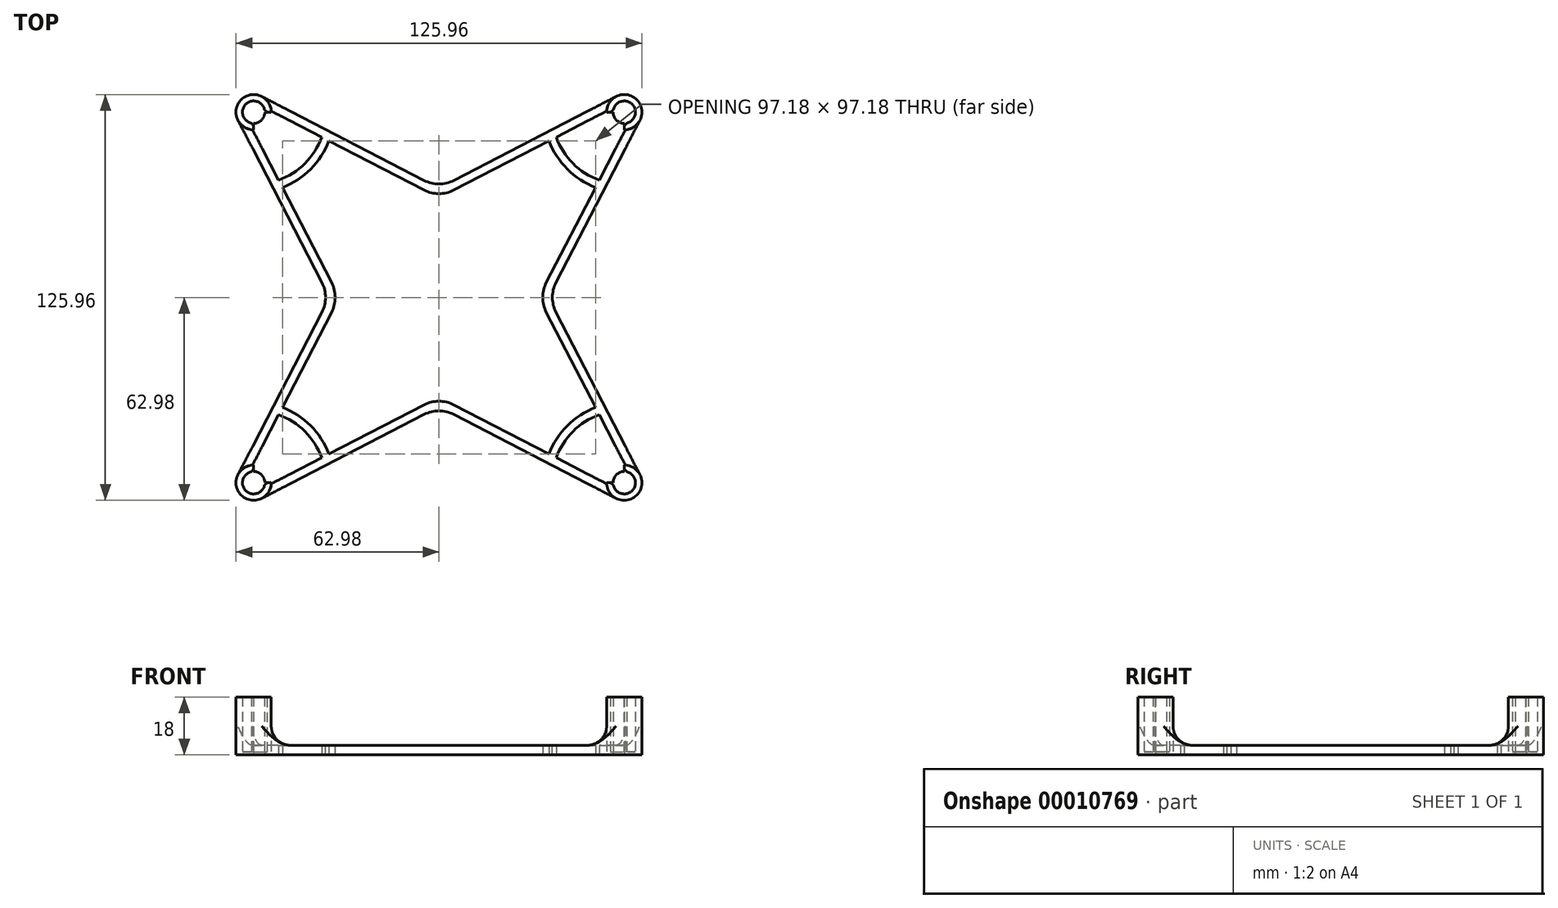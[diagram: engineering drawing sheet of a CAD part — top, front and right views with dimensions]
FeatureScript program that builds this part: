
annotation { "Feature Type Name" : "Feature", "Feature Type Description" : "" }
export const myFeature = defineFeature(function(context is Context, id is Id, definition is map)
    precondition{}
    {
        {
            var Q0;
            Q0=qCreatedBy(makeId("Top.planeOp"),FACE);
            var sketch = newSketch(context, id + "F0", { "sketchPlane" : qUnion([Q0])});
            skLineSegment(sketch, "E0.rect.bottom", {"start": v(57.5, 57.5) * mm, "end": v(-57.5, 57.5) * mm});
            skLineSegment(sketch, "E0.rect.top", {"start": v(57.5, -57.5) * mm, "end": v(-57.5, -57.5) * mm});
            skLineSegment(sketch, "E0.rect.left", {"start": v(57.5, 57.5) * mm, "end": v(57.5, -57.5) * mm});
            skLineSegment(sketch, "E0.rect.right", {"start": v(-57.5, 57.5) * mm, "end": v(-57.5, -57.5) * mm});
            skPoint(sketch, "E0.rect.middle", {"position": v(0, 0) * mm});
            skLineSegment(sketch, "E1", {"start": v(0, 33.94) * mm, "end": v(-33.94, 0) * mm});
            skLineSegment(sketch, "E2", {"start": v(-33.94, 0) * mm, "end": v(0, -33.94) * mm});
            skLineSegment(sketch, "E3", {"start": v(0, -33.94) * mm, "end": v(33.94, 0) * mm});
            skLineSegment(sketch, "E4", {"start": v(33.94, 0) * mm, "end": v(0, 33.94) * mm});
            skCircle(sketch, "E5", {"center": v(57.5, 57.5) * mm, "radius": 3.48 * mm});
            skCircle(sketch, "E6", {"center": v(57.5, 57.5) * mm, "radius": 5.47 * mm});
            skLineSegment(sketch, "E7", {"start": v(57.5, 60.98) * mm, "end": v(57.5, 62.98) * mm, "construction": true});
            skCircle(sketch, "E8", {"center": v(-57.5, 57.5) * mm, "radius": 3.48 * mm});
            skCircle(sketch, "E9", {"center": v(-57.5, 57.5) * mm, "radius": 5.47 * mm});
            skCircle(sketch, "E10", {"center": v(-57.5, -57.5) * mm, "radius": 3.48 * mm});
            skCircle(sketch, "E11", {"center": v(-57.5, -57.5) * mm, "radius": 5.47 * mm});
            skCircle(sketch, "E12", {"center": v(57.5, -57.5) * mm, "radius": 3.48 * mm});
            skCircle(sketch, "E13", {"center": v(57.5, -57.5) * mm, "radius": 5.47 * mm});
            skLineSegment(sketch, "E14", {"start": v(62.36, 54.99) * mm, "end": v(33.94, 0) * mm});
            skLineSegment(sketch, "E15", {"start": v(33.94, 0) * mm, "end": v(62.36, -54.99) * mm});
            skLineSegment(sketch, "E16", {"start": v(54.99, -62.36) * mm, "end": v(0, -33.94) * mm});
            skLineSegment(sketch, "E17", {"start": v(0, -33.94) * mm, "end": v(-54.99, -62.36) * mm});
            skLineSegment(sketch, "E18", {"start": v(-62.36, -54.99) * mm, "end": v(-33.94, 0) * mm});
            skLineSegment(sketch, "E19", {"start": v(-33.94, 0) * mm, "end": v(-62.36, 54.99) * mm});
            skLineSegment(sketch, "E20", {"start": v(-54.99, 62.36) * mm, "end": v(0, 33.94) * mm});
            skLineSegment(sketch, "E21", {"start": v(0, 33.94) * mm, "end": v(54.99, 62.36) * mm});
            skLineSegment(sketch, "E22.0", {"start": v(30.94, 0) * mm, "end": v(0, 30.94) * mm});
            skLineSegment(sketch, "E22.1", {"start": v(0, -30.94) * mm, "end": v(30.94, 0) * mm});
            skLineSegment(sketch, "E22.2", {"start": v(-30.94, 0) * mm, "end": v(0, -30.94) * mm});
            skLineSegment(sketch, "E22.3", {"start": v(0, 30.94) * mm, "end": v(-30.94, 0) * mm});
            skLineSegment(sketch, "E23", {"start": v(-30.94, 0) * mm, "end": v(-57.84, 52.04) * mm});
            skLineSegment(sketch, "E24", {"start": v(-30.94, 0) * mm, "end": v(-57.84, -52.04) * mm});
            skLineSegment(sketch, "E25", {"start": v(30.94, 0) * mm, "end": v(33.94, 0) * mm, "construction": true});
            skLineSegment(sketch, "E26", {"start": v(0, -30.94) * mm, "end": v(-52.04, -57.84) * mm});
            skLineSegment(sketch, "E27", {"start": v(0, -30.94) * mm, "end": v(52.04, -57.84) * mm});
            skLineSegment(sketch, "E28", {"start": v(57.84, -52.04) * mm, "end": v(30.94, 0) * mm});
            skLineSegment(sketch, "E29", {"start": v(30.94, 0) * mm, "end": v(57.84, 52.04) * mm});
            skLineSegment(sketch, "E30", {"start": v(52.04, 57.84) * mm, "end": v(0, 30.94) * mm});
            skLineSegment(sketch, "E31", {"start": v(0, 30.94) * mm, "end": v(-52.04, 57.84) * mm});
            skCircle(sketch, "E32", {"center": v(57.5, 57.5) * mm, "radius": 22.5 * mm});
            skCircle(sketch, "E33", {"center": v(57.5, 57.5) * mm, "radius": 25 * mm});
            skLineSegment(sketch, "E34", {"start": v(57.5, 80) * mm, "end": v(57.5, 82.5) * mm, "construction": true});
            skCircle(sketch, "E35", {"center": v(-57.5, 57.5) * mm, "radius": 22.5 * mm});
            skCircle(sketch, "E36", {"center": v(-57.5, 57.5) * mm, "radius": 25 * mm});
            skCircle(sketch, "E37", {"center": v(-57.5, -57.5) * mm, "radius": 22.5 * mm});
            skCircle(sketch, "E38", {"center": v(-57.5, -57.5) * mm, "radius": 25 * mm});
            skCircle(sketch, "E39", {"center": v(57.5, -57.5) * mm, "radius": 22.5 * mm});
            skCircle(sketch, "E40", {"center": v(57.5, -57.5) * mm, "radius": 25 * mm});
            skSolve(sketch);
        }
        {
            var Q0;
            {var subQ1=sQuery(id+"F0.wireOp",EDGE,"E23");var subQ5=sQuery(id+"F0.wireOp",EDGE,"E0.rect.right");var subQ6=makeQuery(id+"F0.imprint","INTERSECT",VERTEX,{"derivedFrom":[subQ5,subQ1]});Q0=makeQuery(id+"F0.imprint","IMPRINT",FACE,{"disambiguationData":[TD([[makeQuery(id+"F0.imprint","IMPRINT",EDGE,{"disambiguationData":[TD([[subQ6,-1.0]])],"derivedFrom":subQ5}),1.0]])]});}
            var Q1;
            {var subQ1=sQuery(id+"F0.wireOp",EDGE,"E0.rect.right");var subQ5=sQuery(id+"F0.wireOp",EDGE,"E23");var subQ6=makeQuery(id+"F0.imprint","INTERSECT",VERTEX,{"derivedFrom":[subQ1,subQ5]});Q1=makeQuery(id+"F0.imprint","IMPRINT",FACE,{"disambiguationData":[TD([[makeQuery(id+"F0.imprint","IMPRINT",EDGE,{"disambiguationData":[TD([[subQ6,-1.0]])],"derivedFrom":subQ1}),-1.0]])]});}
            var Q2;
            {var subQ0=sQuery(id+"F0.wireOp",EDGE,"E9");var subQ7=sQuery(id+"F0.wireOp",EDGE,"E0.rect.bottom");var subQ8=makeQuery(id+"F0.imprint","INTERSECT",VERTEX,{"derivedFrom":[subQ7,subQ0]});Q2=makeQuery(id+"F0.imprint","IMPRINT",FACE,{"disambiguationData":[TD([[makeQuery(id+"F0.imprint","IMPRINT",EDGE,{"disambiguationData":[TD([[subQ8,-1.0]])],"derivedFrom":subQ7}),-1.0]])]});}
            var Q3;
            {var subQ1=sQuery(id+"F0.wireOp",EDGE,"E0.rect.bottom");var subQ5=sQuery(id+"F0.wireOp",EDGE,"E20");var subQ6=makeQuery(id+"F0.imprint","INTERSECT",VERTEX,{"derivedFrom":[subQ1,subQ5]});Q3=makeQuery(id+"F0.imprint","IMPRINT",FACE,{"disambiguationData":[TD([[makeQuery(id+"F0.imprint","IMPRINT",EDGE,{"disambiguationData":[TD([[subQ6,-1.0]])],"derivedFrom":subQ1}),-1.0]])]});}
            var Q4;
            {var subQ3=sQuery(id+"F0.wireOp",EDGE,"E20");var subQ5=sQuery(id+"F0.wireOp",EDGE,"E0.rect.bottom");var subQ7=makeQuery(id+"F0.imprint","INTERSECT",VERTEX,{"derivedFrom":[subQ5,subQ3]});Q4=makeQuery(id+"F0.imprint","IMPRINT",FACE,{"disambiguationData":[TD([[makeQuery(id+"F0.imprint","IMPRINT",EDGE,{"disambiguationData":[TD([[subQ7,-1.0]])],"derivedFrom":subQ5}),1.0]])]});}
            var Q5;
            {var subQ0=sQuery(id+"F0.wireOp",EDGE,"E36");var subQ3=sQuery(id+"F0.wireOp",EDGE,"E19");var subQ4=makeQuery(id+"F0.imprint","INTERSECT",VERTEX,{"derivedFrom":[subQ3,subQ0]});Q5=makeQuery(id+"F0.imprint","IMPRINT",FACE,{"disambiguationData":[TD([[makeQuery(id+"F0.imprint","IMPRINT",EDGE,{"disambiguationData":[TD([[subQ4,-1.0]])],"derivedFrom":subQ3}),-1.0]])]});}
            var Q6;
            {var subQ1=sQuery(id+"F0.wireOp",EDGE,"E23");var subQ5=sQuery(id+"F0.wireOp",EDGE,"E1");var subQ6=makeQuery(id+"F0.imprint","INTERSECT",VERTEX,{"derivedFrom":[subQ5,subQ1]});Q6=makeQuery(id+"F0.imprint","IMPRINT",FACE,{"disambiguationData":[TD([[makeQuery(id+"F0.imprint","IMPRINT",EDGE,{"disambiguationData":[TD([[subQ6,-1.0]])],"derivedFrom":subQ1}),1.0]])]});}
            var Q7;
            {var subQ3=sQuery(id+"F0.wireOp",EDGE,"E20");var subQ5=sQuery(id+"F0.wireOp",EDGE,"E35");var subQ7=makeQuery(id+"F0.imprint","INTERSECT",VERTEX,{"derivedFrom":[subQ3,subQ5]});Q7=makeQuery(id+"F0.imprint","IMPRINT",FACE,{"disambiguationData":[TD([[makeQuery(id+"F0.imprint","IMPRINT",EDGE,{"disambiguationData":[TD([[subQ7,-1.0]])],"derivedFrom":subQ3}),-1.0]])]});}
            var Q8;
            {var subQ1=sQuery(id+"F0.wireOp",EDGE,"E31");var subQ5=sQuery(id+"F0.wireOp",EDGE,"E1");var subQ6=makeQuery(id+"F0.imprint","INTERSECT",VERTEX,{"derivedFrom":[subQ5,subQ1]});Q8=makeQuery(id+"F0.imprint","IMPRINT",FACE,{"disambiguationData":[TD([[makeQuery(id+"F0.imprint","IMPRINT",EDGE,{"disambiguationData":[TD([[subQ6,-1.0]])],"derivedFrom":subQ1}),-1.0]])]});}
            var Q9;
            {var subQ0=sQuery(id+"F0.wireOp",EDGE,"E31");var subQ1=sQuery(id+"F0.wireOp",EDGE,"E1");var subQ2=makeQuery(id+"F0.imprint","INTERSECT",VERTEX,{"derivedFrom":[subQ1,subQ0]});Q9=makeQuery(id+"F0.imprint","IMPRINT",FACE,{"disambiguationData":[TD([[makeQuery(id+"F0.imprint","IMPRINT",EDGE,{"disambiguationData":[TD([[subQ2,1.0]])],"derivedFrom":subQ1}),1.0]])]});}
            var Q10;
            {var subQ1=sQuery(id+"F0.wireOp",EDGE,"E30");var subQ5=sQuery(id+"F0.wireOp",EDGE,"E4");var subQ6=makeQuery(id+"F0.imprint","INTERSECT",VERTEX,{"derivedFrom":[subQ5,subQ1]});Q10=makeQuery(id+"F0.imprint","IMPRINT",FACE,{"disambiguationData":[TD([[makeQuery(id+"F0.imprint","IMPRINT",EDGE,{"disambiguationData":[TD([[subQ6,1.0]])],"derivedFrom":subQ1}),-1.0]])]});}
            var Q11;
            {var subQ0=sQuery(id+"F0.wireOp",EDGE,"E33");var subQ3=sQuery(id+"F0.wireOp",EDGE,"E21");var subQ4=makeQuery(id+"F0.imprint","INTERSECT",VERTEX,{"derivedFrom":[subQ3,subQ0]});Q11=makeQuery(id+"F0.imprint","IMPRINT",FACE,{"disambiguationData":[TD([[makeQuery(id+"F0.imprint","IMPRINT",EDGE,{"disambiguationData":[TD([[subQ4,-1.0]])],"derivedFrom":subQ3}),-1.0]])]});}
            var Q12;
            {var subQ1=sQuery(id+"F0.wireOp",EDGE,"E30");var subQ5=sQuery(id+"F0.wireOp",EDGE,"E0.rect.bottom");var subQ6=makeQuery(id+"F0.imprint","INTERSECT",VERTEX,{"derivedFrom":[subQ5,subQ1]});Q12=makeQuery(id+"F0.imprint","IMPRINT",FACE,{"disambiguationData":[TD([[makeQuery(id+"F0.imprint","IMPRINT",EDGE,{"disambiguationData":[TD([[subQ6,-1.0]])],"derivedFrom":subQ5}),1.0]])]});}
            var Q13;
            {var subQ0=sQuery(id+"F0.wireOp",EDGE,"E30");var subQ1=sQuery(id+"F0.wireOp",EDGE,"E0.rect.bottom");var subQ2=makeQuery(id+"F0.imprint","INTERSECT",VERTEX,{"derivedFrom":[subQ1,subQ0]});Q13=makeQuery(id+"F0.imprint","IMPRINT",FACE,{"disambiguationData":[TD([[makeQuery(id+"F0.imprint","IMPRINT",EDGE,{"disambiguationData":[TD([[subQ2,-1.0]])],"derivedFrom":subQ1}),-1.0]])]});}
            var Q14;
            {var subQ7=sQuery(id+"F0.wireOp",EDGE,"E5");var subQ9=sQuery(id+"F0.wireOp",EDGE,"E0.rect.bottom");var subQ10=makeQuery(id+"F0.imprint","INTERSECT",VERTEX,{"derivedFrom":[subQ9,subQ7]});Q14=makeQuery(id+"F0.imprint","IMPRINT",FACE,{"disambiguationData":[TD([[makeQuery(id+"F0.imprint","IMPRINT",EDGE,{"disambiguationData":[TD([[subQ10,-1.0]])],"derivedFrom":subQ9}),-1.0]])]});}
            var Q15;
            {var subQ0=sQuery(id+"F0.wireOp",EDGE,"E29");var subQ1=sQuery(id+"F0.wireOp",EDGE,"E0.rect.left");var subQ2=makeQuery(id+"F0.imprint","INTERSECT",VERTEX,{"derivedFrom":[subQ1,subQ0]});Q15=makeQuery(id+"F0.imprint","IMPRINT",FACE,{"disambiguationData":[TD([[makeQuery(id+"F0.imprint","IMPRINT",EDGE,{"disambiguationData":[TD([[subQ2,-1.0]])],"derivedFrom":subQ1}),1.0]])]});}
            var Q16;
            {var subQ1=sQuery(id+"F0.wireOp",EDGE,"E29");var subQ5=sQuery(id+"F0.wireOp",EDGE,"E0.rect.left");var subQ6=makeQuery(id+"F0.imprint","INTERSECT",VERTEX,{"derivedFrom":[subQ5,subQ1]});Q16=makeQuery(id+"F0.imprint","IMPRINT",FACE,{"disambiguationData":[TD([[makeQuery(id+"F0.imprint","IMPRINT",EDGE,{"disambiguationData":[TD([[subQ6,-1.0]])],"derivedFrom":subQ5}),-1.0]])]});}
            var Q17;
            {var subQ3=sQuery(id+"F0.wireOp",EDGE,"E14");var subQ5=sQuery(id+"F0.wireOp",EDGE,"E32");var subQ7=makeQuery(id+"F0.imprint","INTERSECT",VERTEX,{"derivedFrom":[subQ3,subQ5]});Q17=makeQuery(id+"F0.imprint","IMPRINT",FACE,{"disambiguationData":[TD([[makeQuery(id+"F0.imprint","IMPRINT",EDGE,{"disambiguationData":[TD([[subQ7,-1.0]])],"derivedFrom":subQ3}),-1.0]])]});}
            var Q18;
            {var subQ1=sQuery(id+"F0.wireOp",EDGE,"E29");var subQ5=sQuery(id+"F0.wireOp",EDGE,"E4");var subQ6=makeQuery(id+"F0.imprint","INTERSECT",VERTEX,{"derivedFrom":[subQ5,subQ1]});Q18=makeQuery(id+"F0.imprint","IMPRINT",FACE,{"disambiguationData":[TD([[makeQuery(id+"F0.imprint","IMPRINT",EDGE,{"disambiguationData":[TD([[subQ6,-1.0]])],"derivedFrom":subQ1}),-1.0]])]});}
            var Q19;
            {var subQ3=sQuery(id+"F0.wireOp",EDGE,"E28");var subQ5=sQuery(id+"F0.wireOp",EDGE,"E3");var subQ6=makeQuery(id+"F0.imprint","INTERSECT",VERTEX,{"derivedFrom":[subQ5,subQ3]});Q19=makeQuery(id+"F0.imprint","IMPRINT",FACE,{"disambiguationData":[TD([[makeQuery(id+"F0.imprint","IMPRINT",EDGE,{"disambiguationData":[TD([[subQ6,-1.0]])],"derivedFrom":subQ5}),1.0]])]});}
            var Q20;
            {var subQ3=sQuery(id+"F0.wireOp",EDGE,"E23");var subQ5=sQuery(id+"F0.wireOp",EDGE,"E1");var subQ6=makeQuery(id+"F0.imprint","INTERSECT",VERTEX,{"derivedFrom":[subQ5,subQ3]});Q20=makeQuery(id+"F0.imprint","IMPRINT",FACE,{"disambiguationData":[TD([[makeQuery(id+"F0.imprint","IMPRINT",EDGE,{"disambiguationData":[TD([[subQ6,-1.0]])],"derivedFrom":subQ5}),1.0]])]});}
            var Q21;
            {var subQ1=sQuery(id+"F0.wireOp",EDGE,"E24");var subQ5=sQuery(id+"F0.wireOp",EDGE,"E2");var subQ6=makeQuery(id+"F0.imprint","INTERSECT",VERTEX,{"derivedFrom":[subQ5,subQ1]});Q21=makeQuery(id+"F0.imprint","IMPRINT",FACE,{"disambiguationData":[TD([[makeQuery(id+"F0.imprint","IMPRINT",EDGE,{"disambiguationData":[TD([[subQ6,-1.0]])],"derivedFrom":subQ1}),-1.0]])]});}
            var Q22;
            {var subQ1=sQuery(id+"F0.wireOp",EDGE,"E28");var subQ5=sQuery(id+"F0.wireOp",EDGE,"E3");var subQ6=makeQuery(id+"F0.imprint","INTERSECT",VERTEX,{"derivedFrom":[subQ5,subQ1]});Q22=makeQuery(id+"F0.imprint","IMPRINT",FACE,{"disambiguationData":[TD([[makeQuery(id+"F0.imprint","IMPRINT",EDGE,{"disambiguationData":[TD([[subQ6,1.0]])],"derivedFrom":subQ1}),-1.0]])]});}
            var Q23;
            {var subQ0=sQuery(id+"F0.wireOp",EDGE,"E40");var subQ3=sQuery(id+"F0.wireOp",EDGE,"E15");var subQ4=makeQuery(id+"F0.imprint","INTERSECT",VERTEX,{"derivedFrom":[subQ3,subQ0]});Q23=makeQuery(id+"F0.imprint","IMPRINT",FACE,{"disambiguationData":[TD([[makeQuery(id+"F0.imprint","IMPRINT",EDGE,{"disambiguationData":[TD([[subQ4,-1.0]])],"derivedFrom":subQ3}),-1.0]])]});}
            var Q24;
            {var subQ3=sQuery(id+"F0.wireOp",EDGE,"E18");var subQ5=sQuery(id+"F0.wireOp",EDGE,"E37");var subQ7=makeQuery(id+"F0.imprint","INTERSECT",VERTEX,{"derivedFrom":[subQ3,subQ5]});Q24=makeQuery(id+"F0.imprint","IMPRINT",FACE,{"disambiguationData":[TD([[makeQuery(id+"F0.imprint","IMPRINT",EDGE,{"disambiguationData":[TD([[subQ7,-1.0]])],"derivedFrom":subQ3}),-1.0]])]});}
            var Q25;
            {var subQ3=sQuery(id+"F0.wireOp",EDGE,"E18");var subQ5=sQuery(id+"F0.wireOp",EDGE,"E0.rect.right");var subQ7=makeQuery(id+"F0.imprint","INTERSECT",VERTEX,{"derivedFrom":[subQ5,subQ3]});Q25=makeQuery(id+"F0.imprint","IMPRINT",FACE,{"disambiguationData":[TD([[makeQuery(id+"F0.imprint","IMPRINT",EDGE,{"disambiguationData":[TD([[subQ7,-1.0]])],"derivedFrom":subQ5}),1.0]])]});}
            var Q26;
            {var subQ1=sQuery(id+"F0.wireOp",EDGE,"E0.rect.right");var subQ5=sQuery(id+"F0.wireOp",EDGE,"E18");var subQ6=makeQuery(id+"F0.imprint","INTERSECT",VERTEX,{"derivedFrom":[subQ1,subQ5]});Q26=makeQuery(id+"F0.imprint","IMPRINT",FACE,{"disambiguationData":[TD([[makeQuery(id+"F0.imprint","IMPRINT",EDGE,{"disambiguationData":[TD([[subQ6,-1.0]])],"derivedFrom":subQ1}),-1.0]])]});}
            var Q27;
            {var subQ0=sQuery(id+"F0.wireOp",EDGE,"E11");var subQ1=sQuery(id+"F0.wireOp",EDGE,"E0.rect.top");var subQ2=makeQuery(id+"F0.imprint","INTERSECT",VERTEX,{"derivedFrom":[subQ1,subQ0]});Q27=makeQuery(id+"F0.imprint","IMPRINT",FACE,{"disambiguationData":[TD([[makeQuery(id+"F0.imprint","IMPRINT",EDGE,{"disambiguationData":[TD([[subQ2,-1.0]])],"derivedFrom":subQ1}),1.0]])]});}
            var Q28;
            {var subQ1=sQuery(id+"F0.wireOp",EDGE,"E0.rect.top");var subQ5=sQuery(id+"F0.wireOp",EDGE,"E17");var subQ6=makeQuery(id+"F0.imprint","INTERSECT",VERTEX,{"derivedFrom":[subQ1,subQ5]});Q28=makeQuery(id+"F0.imprint","IMPRINT",FACE,{"disambiguationData":[TD([[makeQuery(id+"F0.imprint","IMPRINT",EDGE,{"disambiguationData":[TD([[subQ6,-1.0]])],"derivedFrom":subQ1}),1.0]])]});}
            var Q29;
            {var subQ3=sQuery(id+"F0.wireOp",EDGE,"E17");var subQ5=sQuery(id+"F0.wireOp",EDGE,"E0.rect.top");var subQ7=makeQuery(id+"F0.imprint","INTERSECT",VERTEX,{"derivedFrom":[subQ5,subQ3]});Q29=makeQuery(id+"F0.imprint","IMPRINT",FACE,{"disambiguationData":[TD([[makeQuery(id+"F0.imprint","IMPRINT",EDGE,{"disambiguationData":[TD([[subQ7,-1.0]])],"derivedFrom":subQ5}),-1.0]])]});}
            var Q30;
            {var subQ0=sQuery(id+"F0.wireOp",EDGE,"E38");var subQ3=sQuery(id+"F0.wireOp",EDGE,"E17");var subQ4=makeQuery(id+"F0.imprint","INTERSECT",VERTEX,{"derivedFrom":[subQ3,subQ0]});Q30=makeQuery(id+"F0.imprint","IMPRINT",FACE,{"disambiguationData":[TD([[makeQuery(id+"F0.imprint","IMPRINT",EDGE,{"disambiguationData":[TD([[subQ4,-1.0]])],"derivedFrom":subQ3}),-1.0]])]});}
            var Q31;
            {var subQ1=sQuery(id+"F0.wireOp",EDGE,"E26");var subQ5=sQuery(id+"F0.wireOp",EDGE,"E2");var subQ6=makeQuery(id+"F0.imprint","INTERSECT",VERTEX,{"derivedFrom":[subQ5,subQ1]});Q31=makeQuery(id+"F0.imprint","IMPRINT",FACE,{"disambiguationData":[TD([[makeQuery(id+"F0.imprint","IMPRINT",EDGE,{"disambiguationData":[TD([[subQ6,-1.0]])],"derivedFrom":subQ1}),1.0]])]});}
            var Q32;
            {var subQ3=sQuery(id+"F0.wireOp",EDGE,"E26");var subQ5=sQuery(id+"F0.wireOp",EDGE,"E2");var subQ6=makeQuery(id+"F0.imprint","INTERSECT",VERTEX,{"derivedFrom":[subQ5,subQ3]});Q32=makeQuery(id+"F0.imprint","IMPRINT",FACE,{"disambiguationData":[TD([[makeQuery(id+"F0.imprint","IMPRINT",EDGE,{"disambiguationData":[TD([[subQ6,-1.0]])],"derivedFrom":subQ5}),1.0]])]});}
            var Q33;
            {var subQ1=sQuery(id+"F0.wireOp",EDGE,"E27");var subQ5=sQuery(id+"F0.wireOp",EDGE,"E3");var subQ6=makeQuery(id+"F0.imprint","INTERSECT",VERTEX,{"derivedFrom":[subQ5,subQ1]});Q33=makeQuery(id+"F0.imprint","IMPRINT",FACE,{"disambiguationData":[TD([[makeQuery(id+"F0.imprint","IMPRINT",EDGE,{"disambiguationData":[TD([[subQ6,-1.0]])],"derivedFrom":subQ1}),-1.0]])]});}
            var Q34;
            {var subQ3=sQuery(id+"F0.wireOp",EDGE,"E16");var subQ5=sQuery(id+"F0.wireOp",EDGE,"E39");var subQ7=makeQuery(id+"F0.imprint","INTERSECT",VERTEX,{"derivedFrom":[subQ3,subQ5]});Q34=makeQuery(id+"F0.imprint","IMPRINT",FACE,{"disambiguationData":[TD([[makeQuery(id+"F0.imprint","IMPRINT",EDGE,{"disambiguationData":[TD([[subQ7,-1.0]])],"derivedFrom":subQ3}),-1.0]])]});}
            var Q35;
            {var subQ3=sQuery(id+"F0.wireOp",EDGE,"E0.rect.top");var subQ9=sQuery(id+"F0.wireOp",EDGE,"E12");var subQ11=makeQuery(id+"F0.imprint","INTERSECT",VERTEX,{"derivedFrom":[subQ3,subQ9]});Q35=makeQuery(id+"F0.imprint","IMPRINT",FACE,{"disambiguationData":[TD([[makeQuery(id+"F0.imprint","IMPRINT",EDGE,{"disambiguationData":[TD([[subQ11,-1.0]])],"derivedFrom":subQ3}),1.0]])]});}
            var Q36;
            {var subQ1=sQuery(id+"F0.wireOp",EDGE,"E0.rect.top");var subQ5=sQuery(id+"F0.wireOp",EDGE,"E27");var subQ6=makeQuery(id+"F0.imprint","INTERSECT",VERTEX,{"derivedFrom":[subQ1,subQ5]});Q36=makeQuery(id+"F0.imprint","IMPRINT",FACE,{"disambiguationData":[TD([[makeQuery(id+"F0.imprint","IMPRINT",EDGE,{"disambiguationData":[TD([[subQ6,-1.0]])],"derivedFrom":subQ1}),1.0]])]});}
            var Q37;
            {var subQ1=sQuery(id+"F0.wireOp",EDGE,"E27");var subQ5=sQuery(id+"F0.wireOp",EDGE,"E0.rect.top");var subQ6=makeQuery(id+"F0.imprint","INTERSECT",VERTEX,{"derivedFrom":[subQ5,subQ1]});Q37=makeQuery(id+"F0.imprint","IMPRINT",FACE,{"disambiguationData":[TD([[makeQuery(id+"F0.imprint","IMPRINT",EDGE,{"disambiguationData":[TD([[subQ6,-1.0]])],"derivedFrom":subQ5}),-1.0]])]});}
            var Q38;
            {var subQ1=sQuery(id+"F0.wireOp",EDGE,"E0.rect.left");var subQ5=sQuery(id+"F0.wireOp",EDGE,"E15");var subQ6=makeQuery(id+"F0.imprint","INTERSECT",VERTEX,{"derivedFrom":[subQ1,subQ5]});Q38=makeQuery(id+"F0.imprint","IMPRINT",FACE,{"disambiguationData":[TD([[makeQuery(id+"F0.imprint","IMPRINT",EDGE,{"disambiguationData":[TD([[subQ6,-1.0]])],"derivedFrom":subQ1}),1.0]])]});}
            var Q39;
            {var subQ3=sQuery(id+"F0.wireOp",EDGE,"E15");var subQ5=sQuery(id+"F0.wireOp",EDGE,"E0.rect.left");var subQ7=makeQuery(id+"F0.imprint","INTERSECT",VERTEX,{"derivedFrom":[subQ5,subQ3]});Q39=makeQuery(id+"F0.imprint","IMPRINT",FACE,{"disambiguationData":[TD([[makeQuery(id+"F0.imprint","IMPRINT",EDGE,{"disambiguationData":[TD([[subQ7,-1.0]])],"derivedFrom":subQ5}),-1.0]])]});}
            var Q40;
            {var subQ3=sQuery(id+"F0.wireOp",EDGE,"E23");var subQ5=sQuery(id+"F0.wireOp",EDGE,"E36");var subQ7=makeQuery(id+"F0.imprint","INTERSECT",VERTEX,{"derivedFrom":[subQ3,subQ5]});Q40=makeQuery(id+"F0.imprint","IMPRINT",FACE,{"disambiguationData":[TD([[makeQuery(id+"F0.imprint","IMPRINT",EDGE,{"disambiguationData":[TD([[subQ7,-1.0]])],"derivedFrom":subQ3}),-1.0]])]});}
            var Q41;
            {var subQ0=sQuery(id+"F0.wireOp",EDGE,"E33");var subQ3=sQuery(id+"F0.wireOp",EDGE,"E29");var subQ4=makeQuery(id+"F0.imprint","INTERSECT",VERTEX,{"derivedFrom":[subQ3,subQ0]});Q41=makeQuery(id+"F0.imprint","IMPRINT",FACE,{"disambiguationData":[TD([[makeQuery(id+"F0.imprint","IMPRINT",EDGE,{"disambiguationData":[TD([[subQ4,-1.0]])],"derivedFrom":subQ3}),1.0]])]});}
            var Q42;
            {var subQ0=sQuery(id+"F0.wireOp",EDGE,"E40");var subQ3=sQuery(id+"F0.wireOp",EDGE,"E27");var subQ4=makeQuery(id+"F0.imprint","INTERSECT",VERTEX,{"derivedFrom":[subQ3,subQ0]});Q42=makeQuery(id+"F0.imprint","IMPRINT",FACE,{"disambiguationData":[TD([[makeQuery(id+"F0.imprint","IMPRINT",EDGE,{"disambiguationData":[TD([[subQ4,-1.0]])],"derivedFrom":subQ3}),1.0]])]});}
            var Q43;
            {var subQ0=sQuery(id+"F0.wireOp",EDGE,"E38");var subQ3=sQuery(id+"F0.wireOp",EDGE,"E24");var subQ4=makeQuery(id+"F0.imprint","INTERSECT",VERTEX,{"derivedFrom":[subQ3,subQ0]});Q43=makeQuery(id+"F0.imprint","IMPRINT",FACE,{"disambiguationData":[TD([[makeQuery(id+"F0.imprint","IMPRINT",EDGE,{"disambiguationData":[TD([[subQ4,-1.0]])],"derivedFrom":subQ3}),1.0]])]});}
            extrude(context, id + "F1", {"entities" : qUnion([Q0, Q1, Q2, Q3, Q4, Q5, Q6, Q7, Q8, Q9, Q10, Q11, Q12, Q13, Q14, Q15, Q16, Q17, Q18, Q19, Q20, Q21, Q22, Q23, Q24, Q25, Q26, Q27, Q28, Q29, Q30, Q31, Q32, Q33, Q34, Q35, Q36, Q37, Q38, Q39, Q40, Q41, Q42, Q43]), "depth" : 3 * mm});
        }
        {
            var Q0;
            {var subQ0=sQuery(id+"F0.wireOp",EDGE,"E11");var subQ1=sQuery(id+"F0.wireOp",EDGE,"E0.rect.top");var subQ2=makeQuery(id+"F0.imprint","INTERSECT",VERTEX,{"derivedFrom":[subQ1,subQ0]});Q0=makeQuery(id+"F0.imprint","IMPRINT",FACE,{"disambiguationData":[TD([[makeQuery(id+"F0.imprint","IMPRINT",EDGE,{"disambiguationData":[TD([[subQ2,-1.0]])],"derivedFrom":subQ1}),1.0]])]});}
            var Q1;
            {var subQ0=sQuery(id+"F0.wireOp",EDGE,"E9");var subQ7=sQuery(id+"F0.wireOp",EDGE,"E0.rect.bottom");var subQ8=makeQuery(id+"F0.imprint","INTERSECT",VERTEX,{"derivedFrom":[subQ7,subQ0]});Q1=makeQuery(id+"F0.imprint","IMPRINT",FACE,{"disambiguationData":[TD([[makeQuery(id+"F0.imprint","IMPRINT",EDGE,{"disambiguationData":[TD([[subQ8,-1.0]])],"derivedFrom":subQ7}),-1.0]])]});}
            var Q2;
            {var subQ3=sQuery(id+"F0.wireOp",EDGE,"E0.rect.top");var subQ9=sQuery(id+"F0.wireOp",EDGE,"E12");var subQ11=makeQuery(id+"F0.imprint","INTERSECT",VERTEX,{"derivedFrom":[subQ3,subQ9]});Q2=makeQuery(id+"F0.imprint","IMPRINT",FACE,{"disambiguationData":[TD([[makeQuery(id+"F0.imprint","IMPRINT",EDGE,{"disambiguationData":[TD([[subQ11,-1.0]])],"derivedFrom":subQ3}),1.0]])]});}
            var Q3;
            {var subQ7=sQuery(id+"F0.wireOp",EDGE,"E5");var subQ9=sQuery(id+"F0.wireOp",EDGE,"E0.rect.bottom");var subQ10=makeQuery(id+"F0.imprint","INTERSECT",VERTEX,{"derivedFrom":[subQ9,subQ7]});Q3=makeQuery(id+"F0.imprint","IMPRINT",FACE,{"disambiguationData":[TD([[makeQuery(id+"F0.imprint","IMPRINT",EDGE,{"disambiguationData":[TD([[subQ10,-1.0]])],"derivedFrom":subQ9}),-1.0]])]});}
            extrude(context, id + "F2", {"entities" : qUnion([Q0, Q1, Q2, Q3]), "operationType" : NewBodyOperationType.ADD, "depth" : 18 * mm});
        }
        {
            var Q0;
            {var subQ1=sQuery(id+"F0.wireOp",EDGE,"E0.rect.right");var subQ3=sQuery(id+"F0.wireOp",EDGE,"E0.rect.bottom");var subQ5=makeQuery(id+"F0.imprint","INTERSECT",VERTEX,{"derivedFrom":[subQ3,subQ1]});Q0=makeQuery(id+"F0.imprint","IMPRINT",FACE,{"disambiguationData":[TD([[makeQuery(id+"F0.imprint","IMPRINT",EDGE,{"disambiguationData":[TD([[subQ5,1.0]])],"derivedFrom":subQ3}),-1.0]])]});}
            var Q1;
            {var subQ1=sQuery(id+"F0.wireOp",EDGE,"E0.rect.left");var subQ3=sQuery(id+"F0.wireOp",EDGE,"E0.rect.bottom");var subQ5=makeQuery(id+"F0.imprint","INTERSECT",VERTEX,{"derivedFrom":[subQ3,subQ1]});Q1=makeQuery(id+"F0.imprint","IMPRINT",FACE,{"disambiguationData":[TD([[makeQuery(id+"F0.imprint","IMPRINT",EDGE,{"disambiguationData":[TD([[subQ5,-1.0]])],"derivedFrom":subQ3}),-1.0]])]});}
            var Q2;
            {var subQ1=sQuery(id+"F0.wireOp",EDGE,"E0.rect.left");var subQ3=sQuery(id+"F0.wireOp",EDGE,"E0.rect.top");var subQ5=makeQuery(id+"F0.imprint","INTERSECT",VERTEX,{"derivedFrom":[subQ3,subQ1]});Q2=makeQuery(id+"F0.imprint","IMPRINT",FACE,{"disambiguationData":[TD([[makeQuery(id+"F0.imprint","IMPRINT",EDGE,{"disambiguationData":[TD([[subQ5,-1.0]])],"derivedFrom":subQ3}),1.0]])]});}
            var Q3;
            {var subQ1=sQuery(id+"F0.wireOp",EDGE,"E0.rect.right");var subQ3=sQuery(id+"F0.wireOp",EDGE,"E0.rect.top");var subQ5=makeQuery(id+"F0.imprint","INTERSECT",VERTEX,{"derivedFrom":[subQ3,subQ1]});Q3=makeQuery(id+"F0.imprint","IMPRINT",FACE,{"disambiguationData":[TD([[makeQuery(id+"F0.imprint","IMPRINT",EDGE,{"disambiguationData":[TD([[subQ5,1.0]])],"derivedFrom":subQ3}),1.0]])]});}
            var Q4;
            {var subQ1=sQuery(id+"F0.wireOp",EDGE,"E0.rect.right");var subQ3=sQuery(id+"F0.wireOp",EDGE,"E0.rect.bottom");var subQ5=makeQuery(id+"F0.imprint","INTERSECT",VERTEX,{"derivedFrom":[subQ3,subQ1]});Q4=makeQuery(id+"F0.imprint","IMPRINT",FACE,{"disambiguationData":[TD([[makeQuery(id+"F0.imprint","IMPRINT",EDGE,{"disambiguationData":[TD([[subQ5,1.0]])],"derivedFrom":subQ3}),1.0]])]});}
            var Q5;
            {var subQ1=sQuery(id+"F0.wireOp",EDGE,"E0.rect.left");var subQ3=sQuery(id+"F0.wireOp",EDGE,"E0.rect.bottom");var subQ5=makeQuery(id+"F0.imprint","INTERSECT",VERTEX,{"derivedFrom":[subQ3,subQ1]});Q5=makeQuery(id+"F0.imprint","IMPRINT",FACE,{"disambiguationData":[TD([[makeQuery(id+"F0.imprint","IMPRINT",EDGE,{"disambiguationData":[TD([[subQ5,-1.0]])],"derivedFrom":subQ3}),1.0]])]});}
            var Q6;
            {var subQ1=sQuery(id+"F0.wireOp",EDGE,"E0.rect.left");var subQ3=sQuery(id+"F0.wireOp",EDGE,"E0.rect.top");var subQ5=makeQuery(id+"F0.imprint","INTERSECT",VERTEX,{"derivedFrom":[subQ3,subQ1]});Q6=makeQuery(id+"F0.imprint","IMPRINT",FACE,{"disambiguationData":[TD([[makeQuery(id+"F0.imprint","IMPRINT",EDGE,{"disambiguationData":[TD([[subQ5,-1.0]])],"derivedFrom":subQ3}),-1.0]])]});}
            var Q7;
            {var subQ1=sQuery(id+"F0.wireOp",EDGE,"E0.rect.right");var subQ3=sQuery(id+"F0.wireOp",EDGE,"E0.rect.top");var subQ5=makeQuery(id+"F0.imprint","INTERSECT",VERTEX,{"derivedFrom":[subQ3,subQ1]});Q7=makeQuery(id+"F0.imprint","IMPRINT",FACE,{"disambiguationData":[TD([[makeQuery(id+"F0.imprint","IMPRINT",EDGE,{"disambiguationData":[TD([[subQ5,1.0]])],"derivedFrom":subQ3}),-1.0]])]});}
            extrude(context, id + "F3", {"entities" : qUnion([Q0, Q1, Q2, Q3, Q4, Q5, Q6, Q7]), "operationType" : NewBodyOperationType.ADD, "depth" : 1 * mm});
        }
        {
            var Q0;
            Q0=makeQuery(id+"F1.opExtrude","SWEPT_EDGE",EDGE,{"disambiguationData":[OSD([sQuery(id+"F0.wireOp",EDGE,"E22.2"),sQuery(id+"F0.wireOp",EDGE,"E22.3"),sQuery(id+"F0.wireOp",EDGE,"E23"),sQuery(id+"F0.wireOp",EDGE,"E24")])]});
            var Q1;
            Q1=makeQuery(id+"F1.opExtrude","SWEPT_EDGE",EDGE,{"disambiguationData":[OSD([sQuery(id+"F0.wireOp",EDGE,"E1"),sQuery(id+"F0.wireOp",EDGE,"E2"),sQuery(id+"F0.wireOp",EDGE,"E18"),sQuery(id+"F0.wireOp",EDGE,"E19")])]});
            var Q2;
            Q2=makeQuery(id+"F1.opExtrude","SWEPT_EDGE",EDGE,{"disambiguationData":[OSD([sQuery(id+"F0.wireOp",EDGE,"E22.0"),sQuery(id+"F0.wireOp",EDGE,"E22.3"),sQuery(id+"F0.wireOp",EDGE,"E30"),sQuery(id+"F0.wireOp",EDGE,"E31")])]});
            var Q3;
            Q3=makeQuery(id+"F1.opExtrude","SWEPT_EDGE",EDGE,{"disambiguationData":[OSD([sQuery(id+"F0.wireOp",EDGE,"E1"),sQuery(id+"F0.wireOp",EDGE,"E4"),sQuery(id+"F0.wireOp",EDGE,"E20"),sQuery(id+"F0.wireOp",EDGE,"E21")])]});
            var Q4;
            Q4=makeQuery(id+"F1.opExtrude","SWEPT_EDGE",EDGE,{"disambiguationData":[OSD([sQuery(id+"F0.wireOp",EDGE,"E22.0"),sQuery(id+"F0.wireOp",EDGE,"E22.1"),sQuery(id+"F0.wireOp",EDGE,"E28"),sQuery(id+"F0.wireOp",EDGE,"E29")])]});
            var Q5;
            Q5=makeQuery(id+"F1.opExtrude","SWEPT_EDGE",EDGE,{"disambiguationData":[OSD([sQuery(id+"F0.wireOp",EDGE,"E3"),sQuery(id+"F0.wireOp",EDGE,"E4"),sQuery(id+"F0.wireOp",EDGE,"E14"),sQuery(id+"F0.wireOp",EDGE,"E15")])]});
            var Q6;
            Q6=makeQuery(id+"F1.opExtrude","SWEPT_EDGE",EDGE,{"disambiguationData":[OSD([sQuery(id+"F0.wireOp",EDGE,"E22.1"),sQuery(id+"F0.wireOp",EDGE,"E22.2"),sQuery(id+"F0.wireOp",EDGE,"E26"),sQuery(id+"F0.wireOp",EDGE,"E27")])]});
            var Q7;
            Q7=makeQuery(id+"F1.opExtrude","SWEPT_EDGE",EDGE,{"disambiguationData":[OSD([sQuery(id+"F0.wireOp",EDGE,"E2"),sQuery(id+"F0.wireOp",EDGE,"E3"),sQuery(id+"F0.wireOp",EDGE,"E16"),sQuery(id+"F0.wireOp",EDGE,"E17")])]});
            fillet(context, id + "F4", {"entities" : qUnion([Q0, Q1, Q2, Q3, Q4, Q5, Q6, Q7]), "radius" : 10 * mm, "tangentPropagation" : true, "allowEdgeOverflow" : false});
        }
        {
            var Q0;
            {var subQ0=sQuery(id+"F0.wireOp",EDGE,"E0.rect.bottom");var subQ1=sQuery(id+"F0.wireOp",EDGE,"E8");var subQ2=sQuery(id+"F0.wireOp",EDGE,"E9");Q0=makeQuery(id+"F3.boolean.opBoolean","SPLIT",EDGE,{"disambiguationData":[TD([makeQuery(id+"F2.opExtrude","CAP_FACE",FACE,{"disambiguationData":[OSD([subQ0,sQuery(id+"F0.wireOp",EDGE,"E0.rect.right"),subQ1,subQ2])],"isStart":false})])],"derivedFrom":makeQuery(id+"F2.boolean.opBoolean","MERGE",EDGE,{"derivedFrom":[makeQuery(id+"F1.opExtrude","SWEPT_EDGE",EDGE,{"disambiguationData":[OSD([subQ0,subQ1])]}),makeQuery(id+"F2.opExtrude","SWEPT_EDGE",EDGE,{"disambiguationData":[OSD([subQ0,subQ1])]})]})});}
            var Q1;
            {var subQ0=sQuery(id+"F0.wireOp",EDGE,"E0.rect.right");var subQ1=sQuery(id+"F0.wireOp",EDGE,"E8");var subQ2=sQuery(id+"F0.wireOp",EDGE,"E9");Q1=makeQuery(id+"F3.boolean.opBoolean","SPLIT",EDGE,{"disambiguationData":[TD([makeQuery(id+"F2.opExtrude","CAP_FACE",FACE,{"disambiguationData":[OSD([sQuery(id+"F0.wireOp",EDGE,"E0.rect.bottom"),subQ0,subQ1,subQ2])],"isStart":false})])],"derivedFrom":makeQuery(id+"F2.boolean.opBoolean","MERGE",EDGE,{"derivedFrom":[makeQuery(id+"F1.opExtrude","SWEPT_EDGE",EDGE,{"disambiguationData":[OSD([subQ0,subQ1])]}),makeQuery(id+"F2.opExtrude","SWEPT_EDGE",EDGE,{"disambiguationData":[OSD([subQ0,subQ1])]})]})});}
            var Q2;
            {var subQ0=sQuery(id+"F0.wireOp",EDGE,"E0.rect.bottom");var subQ1=sQuery(id+"F0.wireOp",EDGE,"E5");var subQ2=sQuery(id+"F0.wireOp",EDGE,"E6");Q2=makeQuery(id+"F3.boolean.opBoolean","SPLIT",EDGE,{"disambiguationData":[TD([makeQuery(id+"F2.opExtrude","CAP_FACE",FACE,{"disambiguationData":[OSD([subQ0,sQuery(id+"F0.wireOp",EDGE,"E0.rect.left"),subQ1,subQ2])],"isStart":false})])],"derivedFrom":makeQuery(id+"F2.boolean.opBoolean","MERGE",EDGE,{"derivedFrom":[makeQuery(id+"F1.opExtrude","SWEPT_EDGE",EDGE,{"disambiguationData":[OSD([subQ0,subQ1])]}),makeQuery(id+"F2.opExtrude","SWEPT_EDGE",EDGE,{"disambiguationData":[OSD([subQ0,subQ1])]})]})});}
            var Q3;
            {var subQ0=sQuery(id+"F0.wireOp",EDGE,"E0.rect.left");var subQ1=sQuery(id+"F0.wireOp",EDGE,"E5");var subQ2=sQuery(id+"F0.wireOp",EDGE,"E6");Q3=makeQuery(id+"F3.boolean.opBoolean","SPLIT",EDGE,{"disambiguationData":[TD([makeQuery(id+"F2.opExtrude","CAP_FACE",FACE,{"disambiguationData":[OSD([sQuery(id+"F0.wireOp",EDGE,"E0.rect.bottom"),subQ0,subQ1,subQ2])],"isStart":false})])],"derivedFrom":makeQuery(id+"F2.boolean.opBoolean","MERGE",EDGE,{"derivedFrom":[makeQuery(id+"F1.opExtrude","SWEPT_EDGE",EDGE,{"disambiguationData":[OSD([subQ0,subQ1])]}),makeQuery(id+"F2.opExtrude","SWEPT_EDGE",EDGE,{"disambiguationData":[OSD([subQ0,subQ1])]})]})});}
            var Q4;
            {var subQ0=sQuery(id+"F0.wireOp",EDGE,"E0.rect.top");var subQ1=sQuery(id+"F0.wireOp",EDGE,"E10");var subQ2=sQuery(id+"F0.wireOp",EDGE,"E11");Q4=makeQuery(id+"F3.boolean.opBoolean","SPLIT",EDGE,{"disambiguationData":[TD([makeQuery(id+"F2.opExtrude","CAP_FACE",FACE,{"disambiguationData":[OSD([subQ0,sQuery(id+"F0.wireOp",EDGE,"E0.rect.right"),subQ1,subQ2])],"isStart":false})])],"derivedFrom":makeQuery(id+"F2.boolean.opBoolean","MERGE",EDGE,{"derivedFrom":[makeQuery(id+"F1.opExtrude","SWEPT_EDGE",EDGE,{"disambiguationData":[OSD([subQ0,subQ1])]}),makeQuery(id+"F2.opExtrude","SWEPT_EDGE",EDGE,{"disambiguationData":[OSD([subQ0,subQ1])]})]})});}
            var Q5;
            {var subQ0=sQuery(id+"F0.wireOp",EDGE,"E0.rect.right");var subQ1=sQuery(id+"F0.wireOp",EDGE,"E10");var subQ2=sQuery(id+"F0.wireOp",EDGE,"E11");Q5=makeQuery(id+"F3.boolean.opBoolean","SPLIT",EDGE,{"disambiguationData":[TD([makeQuery(id+"F2.opExtrude","CAP_FACE",FACE,{"disambiguationData":[OSD([sQuery(id+"F0.wireOp",EDGE,"E0.rect.top"),subQ0,subQ1,subQ2])],"isStart":false})])],"derivedFrom":makeQuery(id+"F2.boolean.opBoolean","MERGE",EDGE,{"derivedFrom":[makeQuery(id+"F1.opExtrude","SWEPT_EDGE",EDGE,{"disambiguationData":[OSD([subQ0,subQ1])]}),makeQuery(id+"F2.opExtrude","SWEPT_EDGE",EDGE,{"disambiguationData":[OSD([subQ0,subQ1])]})]})});}
            var Q6;
            {var subQ0=sQuery(id+"F0.wireOp",EDGE,"E0.rect.left");var subQ1=sQuery(id+"F0.wireOp",EDGE,"E12");var subQ2=sQuery(id+"F0.wireOp",EDGE,"E13");Q6=makeQuery(id+"F3.boolean.opBoolean","SPLIT",EDGE,{"disambiguationData":[TD([makeQuery(id+"F2.opExtrude","CAP_FACE",FACE,{"disambiguationData":[OSD([sQuery(id+"F0.wireOp",EDGE,"E0.rect.top"),subQ0,subQ1,subQ2])],"isStart":false})])],"derivedFrom":makeQuery(id+"F2.boolean.opBoolean","MERGE",EDGE,{"derivedFrom":[makeQuery(id+"F1.opExtrude","SWEPT_EDGE",EDGE,{"disambiguationData":[OSD([subQ0,subQ1])]}),makeQuery(id+"F2.opExtrude","SWEPT_EDGE",EDGE,{"disambiguationData":[OSD([subQ0,subQ1])]})]})});}
            var Q7;
            {var subQ0=sQuery(id+"F0.wireOp",EDGE,"E0.rect.top");var subQ1=sQuery(id+"F0.wireOp",EDGE,"E12");var subQ2=sQuery(id+"F0.wireOp",EDGE,"E13");Q7=makeQuery(id+"F3.boolean.opBoolean","SPLIT",EDGE,{"disambiguationData":[TD([makeQuery(id+"F2.opExtrude","CAP_FACE",FACE,{"disambiguationData":[OSD([subQ0,sQuery(id+"F0.wireOp",EDGE,"E0.rect.left"),subQ1,subQ2])],"isStart":false})])],"derivedFrom":makeQuery(id+"F2.boolean.opBoolean","MERGE",EDGE,{"derivedFrom":[makeQuery(id+"F1.opExtrude","SWEPT_EDGE",EDGE,{"disambiguationData":[OSD([subQ0,subQ1])]}),makeQuery(id+"F2.opExtrude","SWEPT_EDGE",EDGE,{"disambiguationData":[OSD([subQ0,subQ1])]})]})});}
            chamfer(context, id + "F5", {"entities" : qUnion([Q0, Q1, Q2, Q3, Q4, Q5, Q6, Q7]), "width" : .9 * mm, "tangentPropagation" : true});
        }
        {
            var Q0;
            {var subQ0=sQuery(id+"F0.wireOp",EDGE,"E6");Q0=makeQuery(id+"F2.boolean.opBoolean","INTERSECT",EDGE,{"disambiguationData":[OD(0.0)],"derivedFrom":[makeQuery(id+"F1.opExtrude","CAP_FACE",FACE,{"disambiguationData":[OSD([sQuery(id+"F0.wireOp",EDGE,"E0.rect.bottom"),sQuery(id+"F0.wireOp",EDGE,"E0.rect.top"),sQuery(id+"F0.wireOp",EDGE,"E0.rect.left"),sQuery(id+"F0.wireOp",EDGE,"E0.rect.right"),sQuery(id+"F0.wireOp",EDGE,"E5"),subQ0,sQuery(id+"F0.wireOp",EDGE,"E8"),sQuery(id+"F0.wireOp",EDGE,"E9"),sQuery(id+"F0.wireOp",EDGE,"E10"),sQuery(id+"F0.wireOp",EDGE,"E11"),sQuery(id+"F0.wireOp",EDGE,"E12"),sQuery(id+"F0.wireOp",EDGE,"E13"),sQuery(id+"F0.wireOp",EDGE,"E14"),sQuery(id+"F0.wireOp",EDGE,"E15"),sQuery(id+"F0.wireOp",EDGE,"E16"),sQuery(id+"F0.wireOp",EDGE,"E17"),sQuery(id+"F0.wireOp",EDGE,"E18"),sQuery(id+"F0.wireOp",EDGE,"E19"),sQuery(id+"F0.wireOp",EDGE,"E20"),sQuery(id+"F0.wireOp",EDGE,"E21"),sQuery(id+"F0.wireOp",EDGE,"E23"),sQuery(id+"F0.wireOp",EDGE,"E24"),sQuery(id+"F0.wireOp",EDGE,"E26"),sQuery(id+"F0.wireOp",EDGE,"E27"),sQuery(id+"F0.wireOp",EDGE,"E28"),sQuery(id+"F0.wireOp",EDGE,"E29"),sQuery(id+"F0.wireOp",EDGE,"E30"),sQuery(id+"F0.wireOp",EDGE,"E31"),sQuery(id+"F0.wireOp",EDGE,"E32"),sQuery(id+"F0.wireOp",EDGE,"E33"),sQuery(id+"F0.wireOp",EDGE,"E35"),sQuery(id+"F0.wireOp",EDGE,"E36"),sQuery(id+"F0.wireOp",EDGE,"E37"),sQuery(id+"F0.wireOp",EDGE,"E38"),sQuery(id+"F0.wireOp",EDGE,"E39"),sQuery(id+"F0.wireOp",EDGE,"E40")])],"isStart":false}),makeQuery(id+"F2.opExtrude","SWEPT_FACE",FACE,{"disambiguationData":[OSD([subQ0])]})]});}
            var Q1;
            {var subQ0=sQuery(id+"F0.wireOp",EDGE,"E6");Q1=makeQuery(id+"F2.boolean.opBoolean","INTERSECT",EDGE,{"disambiguationData":[OD(1.0)],"derivedFrom":[makeQuery(id+"F1.opExtrude","CAP_FACE",FACE,{"disambiguationData":[OSD([sQuery(id+"F0.wireOp",EDGE,"E0.rect.bottom"),sQuery(id+"F0.wireOp",EDGE,"E0.rect.top"),sQuery(id+"F0.wireOp",EDGE,"E0.rect.left"),sQuery(id+"F0.wireOp",EDGE,"E0.rect.right"),sQuery(id+"F0.wireOp",EDGE,"E5"),subQ0,sQuery(id+"F0.wireOp",EDGE,"E8"),sQuery(id+"F0.wireOp",EDGE,"E9"),sQuery(id+"F0.wireOp",EDGE,"E10"),sQuery(id+"F0.wireOp",EDGE,"E11"),sQuery(id+"F0.wireOp",EDGE,"E12"),sQuery(id+"F0.wireOp",EDGE,"E13"),sQuery(id+"F0.wireOp",EDGE,"E14"),sQuery(id+"F0.wireOp",EDGE,"E15"),sQuery(id+"F0.wireOp",EDGE,"E16"),sQuery(id+"F0.wireOp",EDGE,"E17"),sQuery(id+"F0.wireOp",EDGE,"E18"),sQuery(id+"F0.wireOp",EDGE,"E19"),sQuery(id+"F0.wireOp",EDGE,"E20"),sQuery(id+"F0.wireOp",EDGE,"E21"),sQuery(id+"F0.wireOp",EDGE,"E23"),sQuery(id+"F0.wireOp",EDGE,"E24"),sQuery(id+"F0.wireOp",EDGE,"E26"),sQuery(id+"F0.wireOp",EDGE,"E27"),sQuery(id+"F0.wireOp",EDGE,"E28"),sQuery(id+"F0.wireOp",EDGE,"E29"),sQuery(id+"F0.wireOp",EDGE,"E30"),sQuery(id+"F0.wireOp",EDGE,"E31"),sQuery(id+"F0.wireOp",EDGE,"E32"),sQuery(id+"F0.wireOp",EDGE,"E33"),sQuery(id+"F0.wireOp",EDGE,"E35"),sQuery(id+"F0.wireOp",EDGE,"E36"),sQuery(id+"F0.wireOp",EDGE,"E37"),sQuery(id+"F0.wireOp",EDGE,"E38"),sQuery(id+"F0.wireOp",EDGE,"E39"),sQuery(id+"F0.wireOp",EDGE,"E40")])],"isStart":false}),makeQuery(id+"F2.opExtrude","SWEPT_FACE",FACE,{"disambiguationData":[OSD([subQ0])]})]});}
            var Q2;
            {var subQ0=sQuery(id+"F0.wireOp",EDGE,"E9");Q2=makeQuery(id+"F2.boolean.opBoolean","INTERSECT",EDGE,{"disambiguationData":[OD(1.0)],"derivedFrom":[makeQuery(id+"F1.opExtrude","CAP_FACE",FACE,{"disambiguationData":[OSD([sQuery(id+"F0.wireOp",EDGE,"E0.rect.bottom"),sQuery(id+"F0.wireOp",EDGE,"E0.rect.top"),sQuery(id+"F0.wireOp",EDGE,"E0.rect.left"),sQuery(id+"F0.wireOp",EDGE,"E0.rect.right"),sQuery(id+"F0.wireOp",EDGE,"E5"),sQuery(id+"F0.wireOp",EDGE,"E6"),sQuery(id+"F0.wireOp",EDGE,"E8"),subQ0,sQuery(id+"F0.wireOp",EDGE,"E10"),sQuery(id+"F0.wireOp",EDGE,"E11"),sQuery(id+"F0.wireOp",EDGE,"E12"),sQuery(id+"F0.wireOp",EDGE,"E13"),sQuery(id+"F0.wireOp",EDGE,"E14"),sQuery(id+"F0.wireOp",EDGE,"E15"),sQuery(id+"F0.wireOp",EDGE,"E16"),sQuery(id+"F0.wireOp",EDGE,"E17"),sQuery(id+"F0.wireOp",EDGE,"E18"),sQuery(id+"F0.wireOp",EDGE,"E19"),sQuery(id+"F0.wireOp",EDGE,"E20"),sQuery(id+"F0.wireOp",EDGE,"E21"),sQuery(id+"F0.wireOp",EDGE,"E23"),sQuery(id+"F0.wireOp",EDGE,"E24"),sQuery(id+"F0.wireOp",EDGE,"E26"),sQuery(id+"F0.wireOp",EDGE,"E27"),sQuery(id+"F0.wireOp",EDGE,"E28"),sQuery(id+"F0.wireOp",EDGE,"E29"),sQuery(id+"F0.wireOp",EDGE,"E30"),sQuery(id+"F0.wireOp",EDGE,"E31"),sQuery(id+"F0.wireOp",EDGE,"E32"),sQuery(id+"F0.wireOp",EDGE,"E33"),sQuery(id+"F0.wireOp",EDGE,"E35"),sQuery(id+"F0.wireOp",EDGE,"E36"),sQuery(id+"F0.wireOp",EDGE,"E37"),sQuery(id+"F0.wireOp",EDGE,"E38"),sQuery(id+"F0.wireOp",EDGE,"E39"),sQuery(id+"F0.wireOp",EDGE,"E40")])],"isStart":false}),makeQuery(id+"F2.opExtrude","SWEPT_FACE",FACE,{"disambiguationData":[OSD([subQ0])]})]});}
            var Q3;
            {var subQ0=sQuery(id+"F0.wireOp",EDGE,"E9");Q3=makeQuery(id+"F2.boolean.opBoolean","INTERSECT",EDGE,{"disambiguationData":[OD(0.0)],"derivedFrom":[makeQuery(id+"F1.opExtrude","CAP_FACE",FACE,{"disambiguationData":[OSD([sQuery(id+"F0.wireOp",EDGE,"E0.rect.bottom"),sQuery(id+"F0.wireOp",EDGE,"E0.rect.top"),sQuery(id+"F0.wireOp",EDGE,"E0.rect.left"),sQuery(id+"F0.wireOp",EDGE,"E0.rect.right"),sQuery(id+"F0.wireOp",EDGE,"E5"),sQuery(id+"F0.wireOp",EDGE,"E6"),sQuery(id+"F0.wireOp",EDGE,"E8"),subQ0,sQuery(id+"F0.wireOp",EDGE,"E10"),sQuery(id+"F0.wireOp",EDGE,"E11"),sQuery(id+"F0.wireOp",EDGE,"E12"),sQuery(id+"F0.wireOp",EDGE,"E13"),sQuery(id+"F0.wireOp",EDGE,"E14"),sQuery(id+"F0.wireOp",EDGE,"E15"),sQuery(id+"F0.wireOp",EDGE,"E16"),sQuery(id+"F0.wireOp",EDGE,"E17"),sQuery(id+"F0.wireOp",EDGE,"E18"),sQuery(id+"F0.wireOp",EDGE,"E19"),sQuery(id+"F0.wireOp",EDGE,"E20"),sQuery(id+"F0.wireOp",EDGE,"E21"),sQuery(id+"F0.wireOp",EDGE,"E23"),sQuery(id+"F0.wireOp",EDGE,"E24"),sQuery(id+"F0.wireOp",EDGE,"E26"),sQuery(id+"F0.wireOp",EDGE,"E27"),sQuery(id+"F0.wireOp",EDGE,"E28"),sQuery(id+"F0.wireOp",EDGE,"E29"),sQuery(id+"F0.wireOp",EDGE,"E30"),sQuery(id+"F0.wireOp",EDGE,"E31"),sQuery(id+"F0.wireOp",EDGE,"E32"),sQuery(id+"F0.wireOp",EDGE,"E33"),sQuery(id+"F0.wireOp",EDGE,"E35"),sQuery(id+"F0.wireOp",EDGE,"E36"),sQuery(id+"F0.wireOp",EDGE,"E37"),sQuery(id+"F0.wireOp",EDGE,"E38"),sQuery(id+"F0.wireOp",EDGE,"E39"),sQuery(id+"F0.wireOp",EDGE,"E40")])],"isStart":false}),makeQuery(id+"F2.opExtrude","SWEPT_FACE",FACE,{"disambiguationData":[OSD([subQ0])]})]});}
            var Q4;
            {var subQ0=sQuery(id+"F0.wireOp",EDGE,"E11");Q4=makeQuery(id+"F2.boolean.opBoolean","INTERSECT",EDGE,{"disambiguationData":[OD(1.0)],"derivedFrom":[makeQuery(id+"F1.opExtrude","CAP_FACE",FACE,{"disambiguationData":[OSD([sQuery(id+"F0.wireOp",EDGE,"E0.rect.bottom"),sQuery(id+"F0.wireOp",EDGE,"E0.rect.top"),sQuery(id+"F0.wireOp",EDGE,"E0.rect.left"),sQuery(id+"F0.wireOp",EDGE,"E0.rect.right"),sQuery(id+"F0.wireOp",EDGE,"E5"),sQuery(id+"F0.wireOp",EDGE,"E6"),sQuery(id+"F0.wireOp",EDGE,"E8"),sQuery(id+"F0.wireOp",EDGE,"E9"),sQuery(id+"F0.wireOp",EDGE,"E10"),subQ0,sQuery(id+"F0.wireOp",EDGE,"E12"),sQuery(id+"F0.wireOp",EDGE,"E13"),sQuery(id+"F0.wireOp",EDGE,"E14"),sQuery(id+"F0.wireOp",EDGE,"E15"),sQuery(id+"F0.wireOp",EDGE,"E16"),sQuery(id+"F0.wireOp",EDGE,"E17"),sQuery(id+"F0.wireOp",EDGE,"E18"),sQuery(id+"F0.wireOp",EDGE,"E19"),sQuery(id+"F0.wireOp",EDGE,"E20"),sQuery(id+"F0.wireOp",EDGE,"E21"),sQuery(id+"F0.wireOp",EDGE,"E23"),sQuery(id+"F0.wireOp",EDGE,"E24"),sQuery(id+"F0.wireOp",EDGE,"E26"),sQuery(id+"F0.wireOp",EDGE,"E27"),sQuery(id+"F0.wireOp",EDGE,"E28"),sQuery(id+"F0.wireOp",EDGE,"E29"),sQuery(id+"F0.wireOp",EDGE,"E30"),sQuery(id+"F0.wireOp",EDGE,"E31"),sQuery(id+"F0.wireOp",EDGE,"E32"),sQuery(id+"F0.wireOp",EDGE,"E33"),sQuery(id+"F0.wireOp",EDGE,"E35"),sQuery(id+"F0.wireOp",EDGE,"E36"),sQuery(id+"F0.wireOp",EDGE,"E37"),sQuery(id+"F0.wireOp",EDGE,"E38"),sQuery(id+"F0.wireOp",EDGE,"E39"),sQuery(id+"F0.wireOp",EDGE,"E40")])],"isStart":false}),makeQuery(id+"F2.opExtrude","SWEPT_FACE",FACE,{"disambiguationData":[OSD([subQ0])]})]});}
            var Q5;
            {var subQ0=sQuery(id+"F0.wireOp",EDGE,"E11");Q5=makeQuery(id+"F2.boolean.opBoolean","INTERSECT",EDGE,{"disambiguationData":[OD(0.0)],"derivedFrom":[makeQuery(id+"F1.opExtrude","CAP_FACE",FACE,{"disambiguationData":[OSD([sQuery(id+"F0.wireOp",EDGE,"E0.rect.bottom"),sQuery(id+"F0.wireOp",EDGE,"E0.rect.top"),sQuery(id+"F0.wireOp",EDGE,"E0.rect.left"),sQuery(id+"F0.wireOp",EDGE,"E0.rect.right"),sQuery(id+"F0.wireOp",EDGE,"E5"),sQuery(id+"F0.wireOp",EDGE,"E6"),sQuery(id+"F0.wireOp",EDGE,"E8"),sQuery(id+"F0.wireOp",EDGE,"E9"),sQuery(id+"F0.wireOp",EDGE,"E10"),subQ0,sQuery(id+"F0.wireOp",EDGE,"E12"),sQuery(id+"F0.wireOp",EDGE,"E13"),sQuery(id+"F0.wireOp",EDGE,"E14"),sQuery(id+"F0.wireOp",EDGE,"E15"),sQuery(id+"F0.wireOp",EDGE,"E16"),sQuery(id+"F0.wireOp",EDGE,"E17"),sQuery(id+"F0.wireOp",EDGE,"E18"),sQuery(id+"F0.wireOp",EDGE,"E19"),sQuery(id+"F0.wireOp",EDGE,"E20"),sQuery(id+"F0.wireOp",EDGE,"E21"),sQuery(id+"F0.wireOp",EDGE,"E23"),sQuery(id+"F0.wireOp",EDGE,"E24"),sQuery(id+"F0.wireOp",EDGE,"E26"),sQuery(id+"F0.wireOp",EDGE,"E27"),sQuery(id+"F0.wireOp",EDGE,"E28"),sQuery(id+"F0.wireOp",EDGE,"E29"),sQuery(id+"F0.wireOp",EDGE,"E30"),sQuery(id+"F0.wireOp",EDGE,"E31"),sQuery(id+"F0.wireOp",EDGE,"E32"),sQuery(id+"F0.wireOp",EDGE,"E33"),sQuery(id+"F0.wireOp",EDGE,"E35"),sQuery(id+"F0.wireOp",EDGE,"E36"),sQuery(id+"F0.wireOp",EDGE,"E37"),sQuery(id+"F0.wireOp",EDGE,"E38"),sQuery(id+"F0.wireOp",EDGE,"E39"),sQuery(id+"F0.wireOp",EDGE,"E40")])],"isStart":false}),makeQuery(id+"F2.opExtrude","SWEPT_FACE",FACE,{"disambiguationData":[OSD([subQ0])]})]});}
            var Q6;
            {var subQ0=sQuery(id+"F0.wireOp",EDGE,"E13");Q6=makeQuery(id+"F2.boolean.opBoolean","INTERSECT",EDGE,{"disambiguationData":[OD(1.0)],"derivedFrom":[makeQuery(id+"F1.opExtrude","CAP_FACE",FACE,{"disambiguationData":[OSD([sQuery(id+"F0.wireOp",EDGE,"E0.rect.bottom"),sQuery(id+"F0.wireOp",EDGE,"E0.rect.top"),sQuery(id+"F0.wireOp",EDGE,"E0.rect.left"),sQuery(id+"F0.wireOp",EDGE,"E0.rect.right"),sQuery(id+"F0.wireOp",EDGE,"E5"),sQuery(id+"F0.wireOp",EDGE,"E6"),sQuery(id+"F0.wireOp",EDGE,"E8"),sQuery(id+"F0.wireOp",EDGE,"E9"),sQuery(id+"F0.wireOp",EDGE,"E10"),sQuery(id+"F0.wireOp",EDGE,"E11"),sQuery(id+"F0.wireOp",EDGE,"E12"),subQ0,sQuery(id+"F0.wireOp",EDGE,"E14"),sQuery(id+"F0.wireOp",EDGE,"E15"),sQuery(id+"F0.wireOp",EDGE,"E16"),sQuery(id+"F0.wireOp",EDGE,"E17"),sQuery(id+"F0.wireOp",EDGE,"E18"),sQuery(id+"F0.wireOp",EDGE,"E19"),sQuery(id+"F0.wireOp",EDGE,"E20"),sQuery(id+"F0.wireOp",EDGE,"E21"),sQuery(id+"F0.wireOp",EDGE,"E23"),sQuery(id+"F0.wireOp",EDGE,"E24"),sQuery(id+"F0.wireOp",EDGE,"E26"),sQuery(id+"F0.wireOp",EDGE,"E27"),sQuery(id+"F0.wireOp",EDGE,"E28"),sQuery(id+"F0.wireOp",EDGE,"E29"),sQuery(id+"F0.wireOp",EDGE,"E30"),sQuery(id+"F0.wireOp",EDGE,"E31"),sQuery(id+"F0.wireOp",EDGE,"E32"),sQuery(id+"F0.wireOp",EDGE,"E33"),sQuery(id+"F0.wireOp",EDGE,"E35"),sQuery(id+"F0.wireOp",EDGE,"E36"),sQuery(id+"F0.wireOp",EDGE,"E37"),sQuery(id+"F0.wireOp",EDGE,"E38"),sQuery(id+"F0.wireOp",EDGE,"E39"),sQuery(id+"F0.wireOp",EDGE,"E40")])],"isStart":false}),makeQuery(id+"F2.opExtrude","SWEPT_FACE",FACE,{"disambiguationData":[OSD([subQ0])]})]});}
            var Q7;
            {var subQ0=sQuery(id+"F0.wireOp",EDGE,"E13");Q7=makeQuery(id+"F2.boolean.opBoolean","INTERSECT",EDGE,{"disambiguationData":[OD(0.0)],"derivedFrom":[makeQuery(id+"F1.opExtrude","CAP_FACE",FACE,{"disambiguationData":[OSD([sQuery(id+"F0.wireOp",EDGE,"E0.rect.bottom"),sQuery(id+"F0.wireOp",EDGE,"E0.rect.top"),sQuery(id+"F0.wireOp",EDGE,"E0.rect.left"),sQuery(id+"F0.wireOp",EDGE,"E0.rect.right"),sQuery(id+"F0.wireOp",EDGE,"E5"),sQuery(id+"F0.wireOp",EDGE,"E6"),sQuery(id+"F0.wireOp",EDGE,"E8"),sQuery(id+"F0.wireOp",EDGE,"E9"),sQuery(id+"F0.wireOp",EDGE,"E10"),sQuery(id+"F0.wireOp",EDGE,"E11"),sQuery(id+"F0.wireOp",EDGE,"E12"),subQ0,sQuery(id+"F0.wireOp",EDGE,"E14"),sQuery(id+"F0.wireOp",EDGE,"E15"),sQuery(id+"F0.wireOp",EDGE,"E16"),sQuery(id+"F0.wireOp",EDGE,"E17"),sQuery(id+"F0.wireOp",EDGE,"E18"),sQuery(id+"F0.wireOp",EDGE,"E19"),sQuery(id+"F0.wireOp",EDGE,"E20"),sQuery(id+"F0.wireOp",EDGE,"E21"),sQuery(id+"F0.wireOp",EDGE,"E23"),sQuery(id+"F0.wireOp",EDGE,"E24"),sQuery(id+"F0.wireOp",EDGE,"E26"),sQuery(id+"F0.wireOp",EDGE,"E27"),sQuery(id+"F0.wireOp",EDGE,"E28"),sQuery(id+"F0.wireOp",EDGE,"E29"),sQuery(id+"F0.wireOp",EDGE,"E30"),sQuery(id+"F0.wireOp",EDGE,"E31"),sQuery(id+"F0.wireOp",EDGE,"E32"),sQuery(id+"F0.wireOp",EDGE,"E33"),sQuery(id+"F0.wireOp",EDGE,"E35"),sQuery(id+"F0.wireOp",EDGE,"E36"),sQuery(id+"F0.wireOp",EDGE,"E37"),sQuery(id+"F0.wireOp",EDGE,"E38"),sQuery(id+"F0.wireOp",EDGE,"E39"),sQuery(id+"F0.wireOp",EDGE,"E40")])],"isStart":false}),makeQuery(id+"F2.opExtrude","SWEPT_FACE",FACE,{"disambiguationData":[OSD([subQ0])]})]});}
            fillet(context, id + "F6", {"entities" : qUnion([Q0, Q1, Q2, Q3, Q4, Q5, Q6, Q7]), "radius" : 6 * mm, "tangentPropagation" : true, "allowEdgeOverflow" : false});
        }
    });
